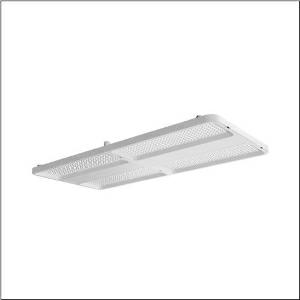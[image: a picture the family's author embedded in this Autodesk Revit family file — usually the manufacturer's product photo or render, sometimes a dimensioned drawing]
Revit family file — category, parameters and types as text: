
# Revit family: highbay_11_maxi_51hn12db3kda
name_source: partatom
category: Lighting Fixtures
units: mm (PartAtom-declared; Revit-internal decimal feet)

## family parameters
Cut with Voids When Loaded = No
Host = Face
Light Source = No
Part Type = Normal
Room Calculation Point = No
Round Connector Dimension = Use Diameter
Shared = No

## types (1)
- --- (1 x LED, 3780 lm, 19.5 W, 3000K)
    Apparent Load = 20 VA
    CIE Flux Codes = 87 98 100 100 100
    Color Rendering = 80
    Color Temperature = 3000K
    Default Elevation = 1800 mm
    Description = high bay luminaire Highbay 11 maxi; direct symmetric wide distribution, light control with lens of PMMA; UGR ≤ 19 (X = 4H | Y = 8H | S = 0.25H | reflection values 70/50/20); luminous flux: 24.700lm; light colour: 830, colour temperature: 3000K, MacAdam ≤ 2 SDCM (initial), colour rendering: CRI > 80; luminous efficacy: 197,1lm/W; rated service life: 100.000h (L95/B50) at AT= 25°C; control: DALI 2; luminaire connection: terminal, 5-pole, max. 2.5mm² (cable entry for one cable, Ø 8.5..16mm); mains connection: 230..240V, AC/DC 0/50..60Hz; connected load: 125,3W; protection rating (complete): IP66; insulation class (complete): insulation class I (protective earthing); protection symbol: D; impact resistance: IK08; certification: CE, ENEC, VDE, UKCA; luminaire for central battery installations according to DIN EN 60598-2-22, internal wiring halogen-free; luminaire LABS conformity tested according to VDMA 24364:2018-05; corresponds to IFS (International Featured Standards) requirements for safety and quality in the food industry; housing frame of high-performance plastic PA6, matt traffic white (RAL 9016); cover of PMMA; dimension (LxWxH): 946 x 442 x 72mm; permissible operating ambient temperature: -40..+65°C (reducing of maximum allowable ambient temperature of 5°C with ceiling mounting); packaging unit: 1 piece; (delivery without accessories; please order mounting accessories separately)
    Height = 72 mm  [stored 0.23622 ft]
    Lamp = 1 x LED
    Lamp Light Flux = 3780 lm
    Lamp Power = 19.5 W
    Lamp count = 1
    Length = 946 mm
    Luminous efficacy = 194 lm/W
    Manufacturer = Siteco
    ModVariant = No
    Model = 51HN12DB3KDA
    Mounting Place = Ceiling
    Mounting Type = Pendant
    Number of Poles = 1
    OnlyDefault = Yes
    Power Factor = 1
    Product Name = Highbay 11 maxi
    Product group = high bay luminaire
    ProductGroupID = 901
    Protection Class = Protection class I
    Protection Degree = IP 66
    RLX_Detail_Level = 1
    RLX_Emergency_Light_Flux = 0 lm
    RLX_Emergency_Type = 0
    RLX_Emergency_Type_DB = No
    RlxData = <blob elided: 127329 chars, md5=3ecc478a>
    Socket = socket
    Standby Power = 0 W
    System Light Flux = 3780 lm
    System Power = 20 W
    Type Comments = : DC mode (central or group accumulator) initial emergency light level
    Type Image = l_1363244.jpg
    URL = http://relux.com
    VarID = @adj_000617
    Voltage = 0 V
    Weight = 0.00 kg
    Width = 442 mm

note: [stored X ft] marks values corroborated as IEEE doubles in the binary element streams (Revit-internal decimal feet)

## geometry (parser evidence)
native form markers: Blend x4, Sweep x12
no freeform markers — native parametric forms only
